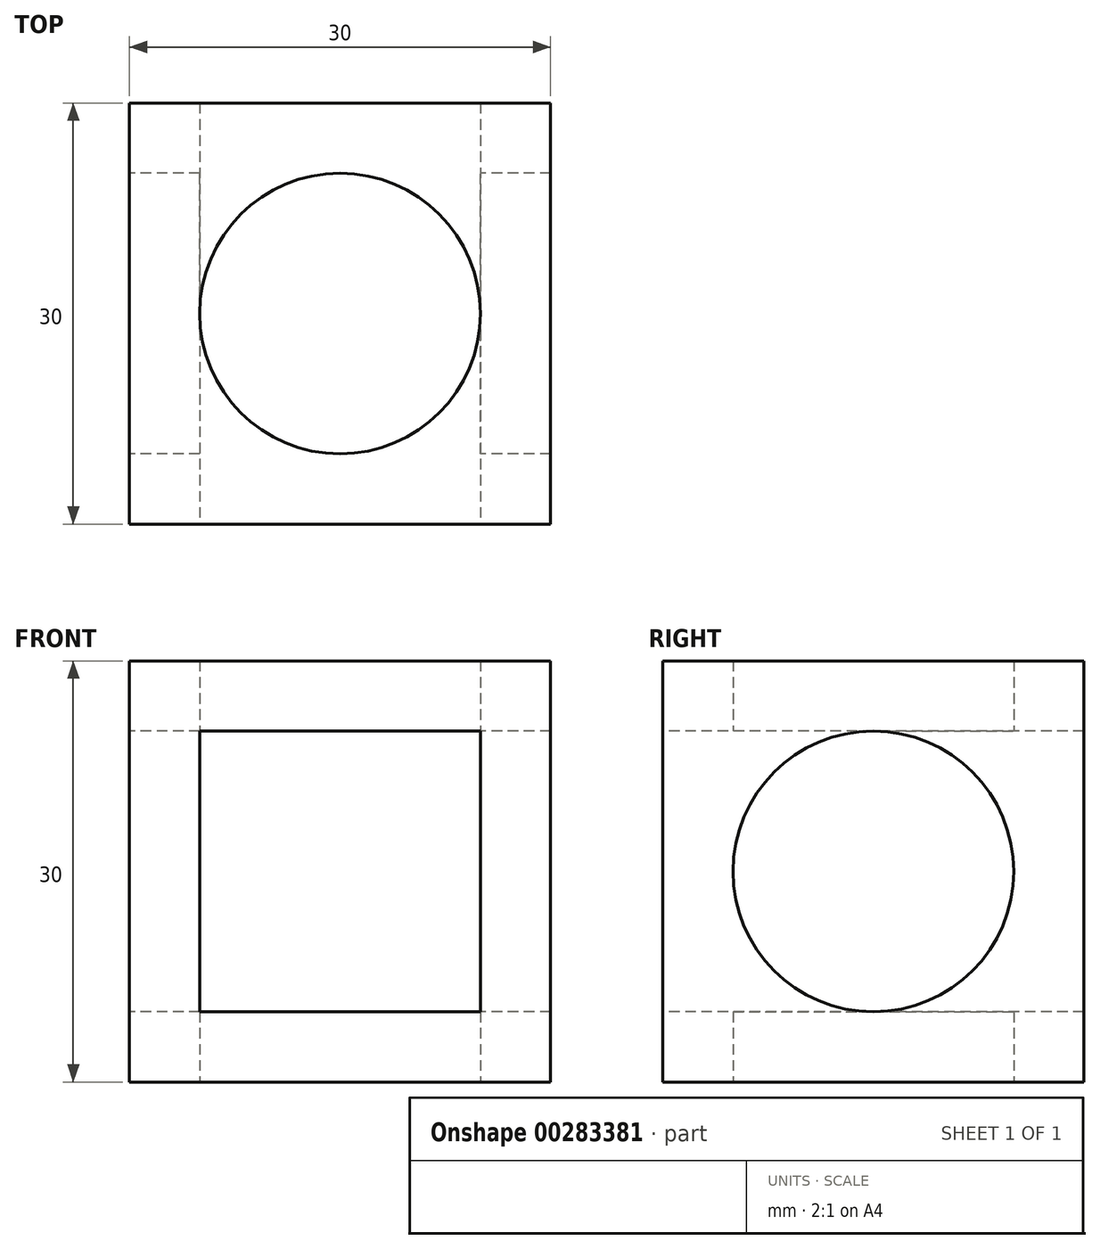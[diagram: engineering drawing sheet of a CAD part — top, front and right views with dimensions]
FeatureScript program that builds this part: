
annotation { "Feature Type Name" : "Feature", "Feature Type Description" : "" }
export const myFeature = defineFeature(function(context is Context, id is Id, definition is map)
    precondition{}
    {
        {
            var Q0;
            Q0=qCreatedBy(makeId("Top.planeOp"),FACE);
            var sketch = newSketch(context, id + "F0", { "sketchPlane" : qUnion([Q0])});
            skLineSegment(sketch, "E0.bottom", {"start": v(15, 15) * mm, "end": v(-15, 15) * mm});
            skLineSegment(sketch, "E0.top", {"start": v(15, -15) * mm, "end": v(-15, -15) * mm});
            skLineSegment(sketch, "E0.left", {"start": v(15, 15) * mm, "end": v(15, -15) * mm});
            skLineSegment(sketch, "E0.right", {"start": v(-15, 15) * mm, "end": v(-15, -15) * mm});
            skPoint(sketch, "E0.middle", {"position": v(0, 0) * mm});
            skSolve(sketch);
        }
        {
            var Q0;
            Q0 = qSketchRegion(id + "F0", true);
            extrude(context, id + "F1", {"entities" : qUnion([Q0]), "depth" : 30 * mm});
        }
        {
            var Q0;
            Q0=qCreatedBy(makeId("Top.planeOp"),FACE);
            var sketch = newSketch(context, id + "F2", { "sketchPlane" : qUnion([Q0])});
            skCircle(sketch, "E1", {"center": v(0, 0) * mm, "radius": 10 * mm});
            skSolve(sketch);
        }
        {
            var Q0;
            Q0=sQuery(id+"F2.wireOp",VERTEX,"E1.center");
            var Q1;
            Q1=makeQuery(id+"F1.opExtrude","SWEPT_BODY",BODY,{"disambiguationData":[OSD([sQuery(id+"F0.wireOp",EDGE,"E0.bottom"),sQuery(id+"F0.wireOp",EDGE,"E0.top"),sQuery(id+"F0.wireOp",EDGE,"E0.left"),sQuery(id+"F0.wireOp",EDGE,"E0.right")])]});
            hole(context, id + "F3", {"style" : HoleStyle.SIMPLE, "endStyle" : HoleEndStyle.THROUGH, "oppositeDirection" : true, "holeDiameter" : 20 * mm, "tappedDepth" : 12.7 * mm, "tapClearance" : 3, "locations" : qUnion([Q0]), "scope" : qUnion([Q1])});
        }
        {
            var Q0;
            Q0=makeQuery(id+"F1.opExtrude","SWEPT_FACE",FACE,{"disambiguationData":[OSD([sQuery(id+"F0.wireOp",EDGE,"E0.right")])]});
            var sketch = newSketch(context, id + "F4", { "sketchPlane" : qUnion([Q0])});
            skCircle(sketch, "E2", {"center": v(0, 15) * mm, "radius": 15 * mm});
            skPoint(sketch, "E2.first.point", {"position": v(0, 30) * mm});
            skPoint(sketch, "E2.second.point", {"position": v(15, 15) * mm});
            skPoint(sketch, "E2.third.point", {"position": v(-15, 15) * mm});
            skCircle(sketch, "E3", {"center": v(0, 15) * mm, "radius": 10 * mm});
            skSolve(sketch);
        }
        {
            var Q0;
            Q0=sQuery(id+"F4.wireOp",VERTEX,"E2.center");
            var Q1;
            Q1=makeQuery(id+"F1.opExtrude","SWEPT_BODY",BODY,{"disambiguationData":[OSD([sQuery(id+"F0.wireOp",EDGE,"E0.bottom"),sQuery(id+"F0.wireOp",EDGE,"E0.top"),sQuery(id+"F0.wireOp",EDGE,"E0.left"),sQuery(id+"F0.wireOp",EDGE,"E0.right")])]});
            hole(context, id + "F5", {"style" : HoleStyle.SIMPLE, "endStyle" : HoleEndStyle.THROUGH, "holeDiameter" : 20 * mm, "tappedDepth" : 12.7 * mm, "tapClearance" : 3, "locations" : qUnion([Q0]), "scope" : qUnion([Q1])});
        }
        {
            var Q0;
            Q0=makeQuery(id+"F1.opExtrude","SWEPT_FACE",FACE,{"disambiguationData":[OSD([sQuery(id+"F0.wireOp",EDGE,"E0.top")])]});
            var sketch = newSketch(context, id + "F6", { "sketchPlane" : qUnion([Q0])});
            skCircle(sketch, "E4", {"center": v(0, 15) * mm, "radius": 15 * mm});
            skPoint(sketch, "E4.first.point", {"position": v(0, 30) * mm});
            skPoint(sketch, "E4.second.point", {"position": v(-15, 15) * mm});
            skPoint(sketch, "E4.third.point", {"position": v(15, 15) * mm});
            skLineSegment(sketch, "E5.bottom", {"start": v(10, 25) * mm, "end": v(-10, 25) * mm});
            skLineSegment(sketch, "E5.top", {"start": v(10, 5) * mm, "end": v(-10, 5) * mm});
            skLineSegment(sketch, "E5.left", {"start": v(10, 25) * mm, "end": v(10, 5) * mm});
            skLineSegment(sketch, "E5.right", {"start": v(-10, 25) * mm, "end": v(-10, 5) * mm});
            skSolve(sketch);
        }
        {
            var Q0;
            Q0=makeQuery(id+"F6.imprint","IMPRINT",FACE,{"disambiguationData":[TD([[makeQuery(id+"F6.imprint","IMPRINT",EDGE,{"derivedFrom":sQuery(id+"F6.wireOp",EDGE,"E5.bottom")}),1.0]])]});
            extrude(context, id + "F7", {"entities" : qUnion([Q0]), "operationType" : NewBodyOperationType.REMOVE, "oppositeDirection" : true, "depth" : 30 * mm});
        }
    });
